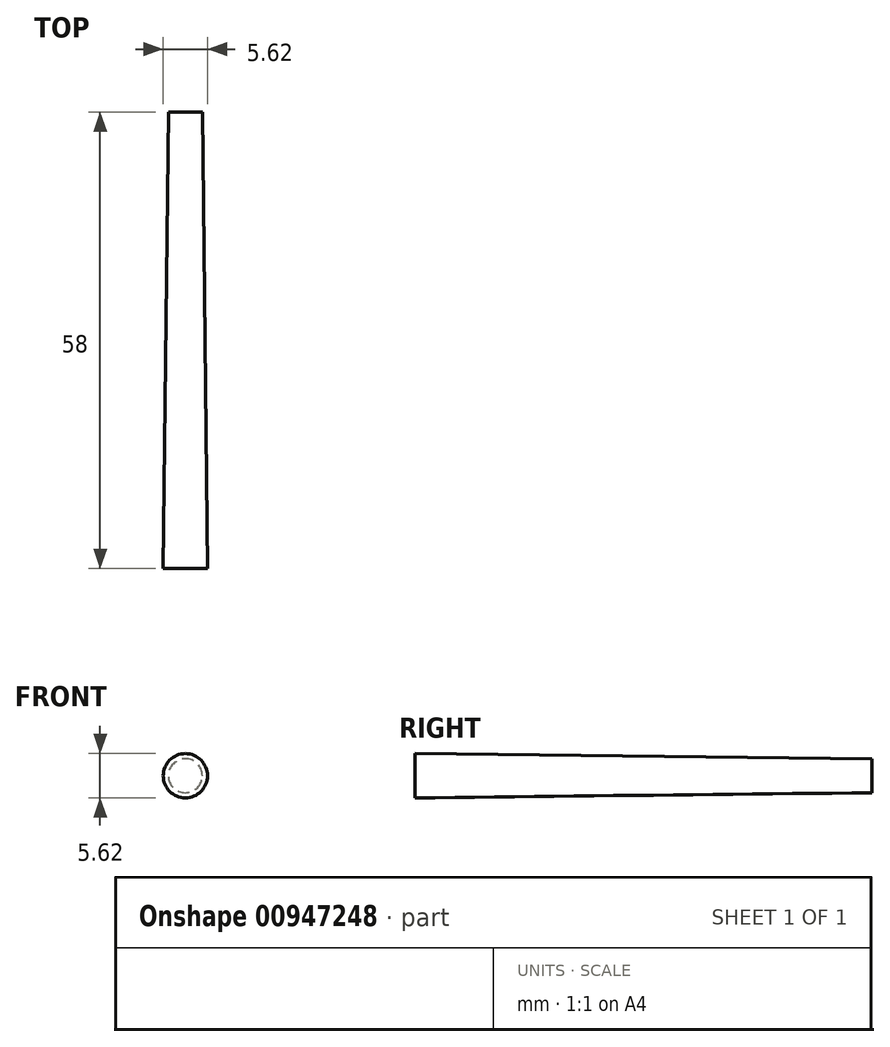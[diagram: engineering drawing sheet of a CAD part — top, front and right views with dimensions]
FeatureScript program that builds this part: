
annotation { "Feature Type Name" : "Feature", "Feature Type Description" : "" }
export const myFeature = defineFeature(function(context is Context, id is Id, definition is map)
    precondition{}
    {
        {
            var Q0;
            Q0=qCreatedBy(makeId("Front.planeOp"),FACE);
            cPlane(context, id + "F0", {"entities" : qUnion([Q0]), "cplaneType" : CPlaneType.OFFSET, "offset" : 29 * mm, "width" : 150 * mm, "height" : 150 * mm});
        }
        {
            var Q0;
            Q0=qCreatedBy(id+"F0.planeOp",FACE);
            var sketch = newSketch(context, id + "F1", { "sketchPlane" : qUnion([Q0])});
            skCircle(sketch, "E0", {"center": v(0, 0) * mm, "radius": 2.81 * mm});
            skSolve(sketch);
        }
        {
            var Q0;
            Q0=qCreatedBy(makeId("Front.planeOp"),FACE);
            cPlane(context, id + "F2", {"entities" : qUnion([Q0]), "cplaneType" : CPlaneType.OFFSET, "offset" : 29 * mm, "oppositeDirection" : true, "width" : 150 * mm, "height" : 150 * mm});
        }
        {
            var Q0;
            Q0=qCreatedBy(id+"F2.planeOp",FACE);
            var sketch = newSketch(context, id + "F3", { "sketchPlane" : qUnion([Q0])});
            skCircle(sketch, "E1", {"center": v(0, 0) * mm, "radius": 2.15 * mm});
            skSolve(sketch);
        }
        {
            var Q0;
            Q0=makeQuery(id+"F1.imprint","IMPRINT",FACE,{"disambiguationData":[TD([[makeQuery(id+"F1.imprint","IMPRINT",EDGE,{"derivedFrom":sQuery(id+"F1.wireOp",EDGE,"E0")}),1.0]])]});
            var Q1;
            Q1=makeQuery(id+"F3.imprint","IMPRINT",FACE,{"disambiguationData":[TD([[makeQuery(id+"F3.imprint","IMPRINT",EDGE,{"derivedFrom":sQuery(id+"F3.wireOp",EDGE,"E1")}),1.0]])]});
            loft(context, id + "F4", {"sheetProfilesArray" : [{ "sheetProfileEntities" : qUnion([Q0]) }, { "sheetProfileEntities" : qUnion([Q1]) }]});
        }
    });
